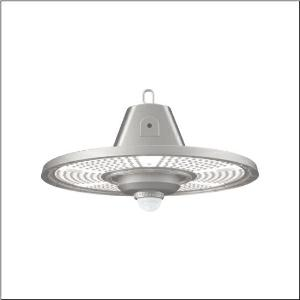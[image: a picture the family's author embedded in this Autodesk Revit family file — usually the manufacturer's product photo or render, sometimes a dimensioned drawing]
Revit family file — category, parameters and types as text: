
# Revit family: highbay_31-l_51hc427a4mmb01
name_source: partatom
category: Lighting Fixtures
units: mm (PartAtom-declared; Revit-internal decimal feet)

## family parameters
Cut with Voids When Loaded = No
Host = Face
Light Source = No
Part Type = Normal
Room Calculation Point = No
Round Connector Dimension = Use Diameter
Shared = No

## types (1)
- Highbay 31-L (1 x LED, 28000 lm, 187 W, 4000K)
    Apparent Load = 187 VA
    CIE Flux Codes = 83 98 100 100 100
    Color Rendering = 80
    Color Temperature = 4000K
    Default Elevation = 1800 mm
    Description = Highbay 31-L, LED high bay luminaire, primary light control with lens, of PC, primary optical cover: cover panel, of PC, transparent, light emission: direct distribution, primary light characteristic: rotationally symmetric, installation type: suspended mounting, surface-mounted, LED, rated luminous flux: 28.000lm, luminous efficacy: 150lm/W, light colour: 840, colour temperature: 4000K, control gear: ECG, with cable, 3x 1.0mm², free wire ends, mains connection: 220..240V, AC/DC, 0/50..60Hz, cable length: 1,5m, rated input power: 187W, housing, rotationally symmetric, of diecast aluminium, powder-coated, grey aluminium (RAL 9007), with hook on luminaire side, incl. screw, diameter: 406mm, PIR sensor, protection rating (complete): IP65, insulation class (complete): insulation class I (protective earthing), certification: CE, ENEC, UKCA, protection symbol: D, impact resistance: IK08, permissible operating ambient temperature: -30..+45°C, standard: EN 60598-2-22, EN 60598, corresponds to IFS (International Featured Standards) requirements for safety and quality in the food industry, packaging unit: 1 piece
    Height = 160 mm
    Lamp = 1 x LED
    Lamp Light Flux = 28000 lm
    Lamp Power = 187 W
    Lamp count = 1
    Length = 406 mm
    Luminous efficacy = 150 lm/W
    Manufacturer = Siteco
    ModVariant = No
    Model = 51HC427A4MMB01
    Mounting Place = Ceiling
    Mounting Type = Pendant
    Number of Poles = 1
    OnlyDefault = Yes
    Power Factor = 1
    Product Name = Highbay 31-L
    Product group = LED high bay luminaire
    ProductGroupID = 903
    Protection Class = Protection class I
    Protection Degree = IP 65
    RLX_Detail_Level = 1
    RLX_Emergency_Light_Flux = 0 lm
    RLX_Emergency_Type = 0
    RLX_Emergency_Type_DB = No
    RlxData = <blob elided: 121701 chars, md5=75d184b1>
    Socket = socket
    Standby Power = 0 W
    System Light Flux = 28000 lm
    System Power = 187 W
    Type Comments = Product without accessories
    Type Image = l_384981.jpg
    URL = http://relux.com
    VarID = ---
    Voltage = 0 V
    Weight = 0.00 kg
    Width = 0 mm  [stored 0 ft]

note: [stored X ft] marks values corroborated as IEEE doubles in the binary element streams (Revit-internal decimal feet)

## geometry (parser evidence)
native form markers: Blend x4, Sweep x12
no freeform markers — native parametric forms only
